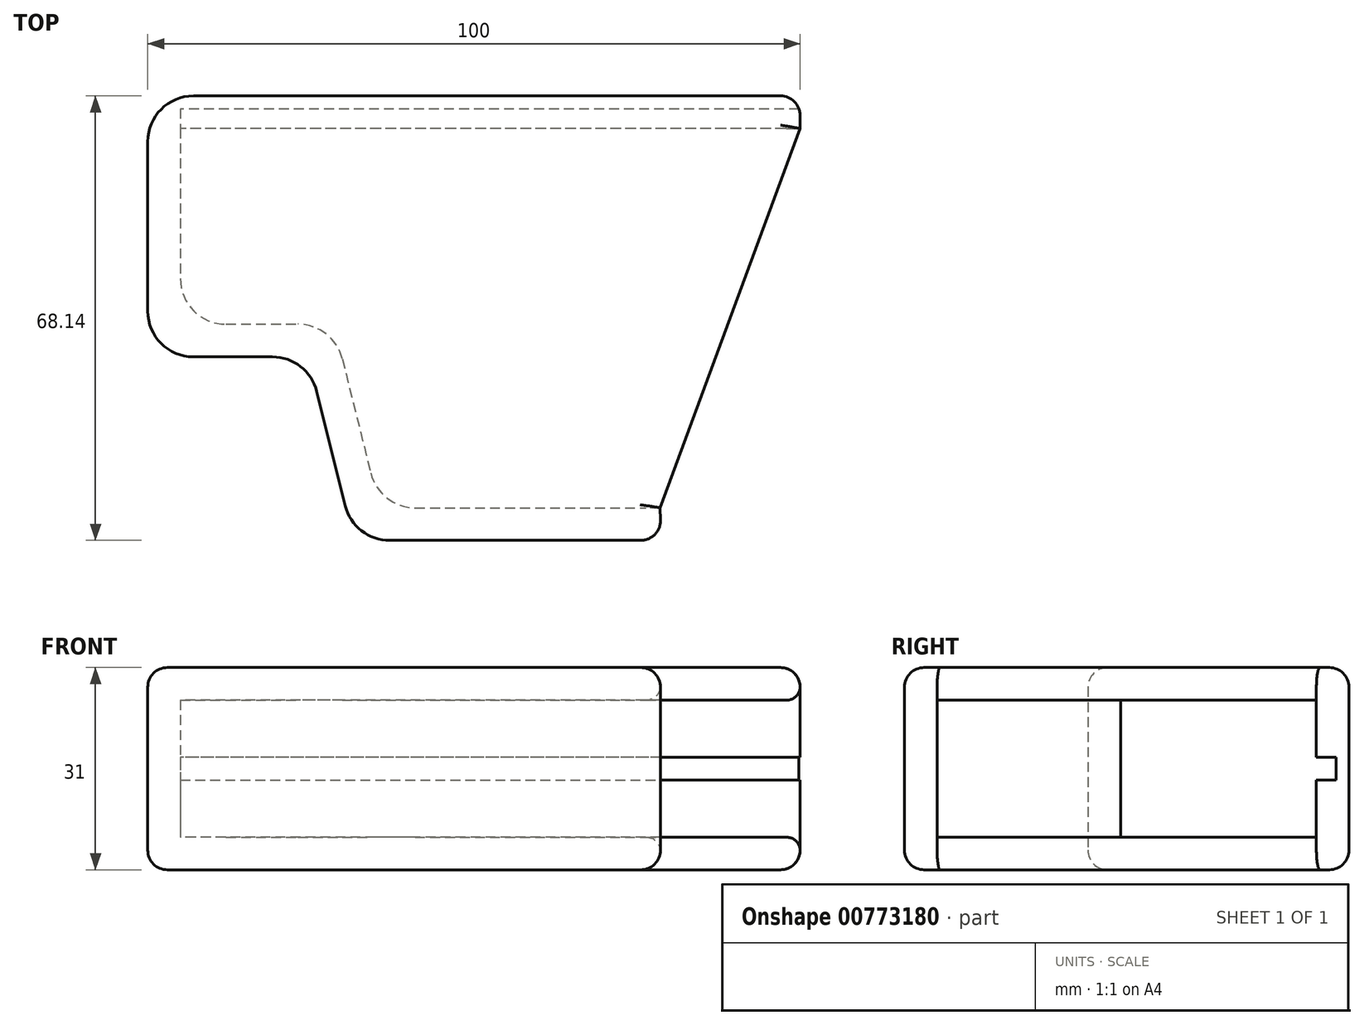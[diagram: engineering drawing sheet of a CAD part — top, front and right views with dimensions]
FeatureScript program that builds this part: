
annotation { "Feature Type Name" : "Feature", "Feature Type Description" : "" }
export const myFeature = defineFeature(function(context is Context, id is Id, definition is map)
    precondition{}
    {
        {
            var Q0;
            Q0=qCreatedBy(makeId("Top.planeOp"),FACE);
            var sketch = newSketch(context, id + "F0", { "sketchPlane" : qUnion([Q0])});
            skLineSegment(sketch, "E0", {"start": v(71.5, 30) * mm, "end": v(-23.5, 30) * mm});
            skLineSegment(sketch, "E1", {"start": v(-23.5, 30) * mm, "end": v(-23.5, 0) * mm});
            skLineSegment(sketch, "E2", {"start": v(-23.5, 0) * mm, "end": v(0, 0) * mm});
            skLineSegment(sketch, "E3", {"start": v(0, 0) * mm, "end": v(7.01, -28.14) * mm});
            skLineSegment(sketch, "E4", {"start": v(7.01, -28.14) * mm, "end": v(50.01, -28.14) * mm});
            skLineSegment(sketch, "E5", {"start": v(71.5, 30) * mm, "end": v(71.5, 35) * mm});
            skLineSegment(sketch, "E6", {"start": v(71.5, 35) * mm, "end": v(-28.5, 35) * mm});
            skLineSegment(sketch, "E7", {"start": v(-28.5, 35) * mm, "end": v(-28.5, -5) * mm});
            skLineSegment(sketch, "E8", {"start": v(-28.5, -5) * mm, "end": v(-3.9, -5) * mm});
            skLineSegment(sketch, "E9", {"start": v(-3.9, -5) * mm, "end": v(3.1, -33.14) * mm});
            skLineSegment(sketch, "E10", {"start": v(3.1, -33.14) * mm, "end": v(50.2, -33.14) * mm});
            skLineSegment(sketch, "E11", {"start": v(50.2, -33.14) * mm, "end": v(50.01, -28.14) * mm});
            skSolve(sketch);
        }
        {
            var Q0;
            Q0 = qSketchRegion(id + "F0", true);
            extrude(context, id + "F1", {"entities" : qUnion([Q0]), "depth" : 21 * mm, "offsetDistance" : 25 * mm});
        }
        {
            var Q0;
            Q0=makeQuery(id+"F1.opExtrude","CAP_FACE",FACE,{"disambiguationData":[OSD([sQuery(id+"F0.wireOp",EDGE,"E0"),sQuery(id+"F0.wireOp",EDGE,"E1"),sQuery(id+"F0.wireOp",EDGE,"E2"),sQuery(id+"F0.wireOp",EDGE,"E3"),sQuery(id+"F0.wireOp",EDGE,"E4"),sQuery(id+"F0.wireOp",EDGE,"E5"),sQuery(id+"F0.wireOp",EDGE,"E6"),sQuery(id+"F0.wireOp",EDGE,"E7"),sQuery(id+"F0.wireOp",EDGE,"E8"),sQuery(id+"F0.wireOp",EDGE,"E9"),sQuery(id+"F0.wireOp",EDGE,"E10"),sQuery(id+"F0.wireOp",EDGE,"E11")])],"isStart":true});
            var sketch = newSketch(context, id + "F2", { "sketchPlane" : qUnion([Q0])});
            skLineSegment(sketch, "E12", {"start": v(71.5, -35) * mm, "end": v(-28.5, -35) * mm});
            skLineSegment(sketch, "E13", {"start": v(-28.5, -35) * mm, "end": v(-28.5, 5) * mm});
            skLineSegment(sketch, "E14", {"start": v(-28.5, 5) * mm, "end": v(-3.9, 5) * mm});
            skLineSegment(sketch, "E15", {"start": v(-3.9, 5) * mm, "end": v(3.1, 33.14) * mm});
            skLineSegment(sketch, "E16", {"start": v(3.1, 33.14) * mm, "end": v(50.2, 33.14) * mm});
            skLineSegment(sketch, "E17", {"start": v(50.2, 33.14) * mm, "end": v(50.01, 28.14) * mm});
            skLineSegment(sketch, "E18", {"start": v(50.01, 28.14) * mm, "end": v(71.5, -30) * mm});
            skLineSegment(sketch, "E19", {"start": v(71.5, -30) * mm, "end": v(71.5, -35) * mm});
            skSolve(sketch);
        }
        {
            var Q0;
            Q0=makeQuery(id+"F1.opExtrude","CAP_FACE",FACE,{"disambiguationData":[OSD([sQuery(id+"F0.wireOp",EDGE,"E0"),sQuery(id+"F0.wireOp",EDGE,"E1"),sQuery(id+"F0.wireOp",EDGE,"E2"),sQuery(id+"F0.wireOp",EDGE,"E3"),sQuery(id+"F0.wireOp",EDGE,"E4"),sQuery(id+"F0.wireOp",EDGE,"E5"),sQuery(id+"F0.wireOp",EDGE,"E6"),sQuery(id+"F0.wireOp",EDGE,"E7"),sQuery(id+"F0.wireOp",EDGE,"E8"),sQuery(id+"F0.wireOp",EDGE,"E9"),sQuery(id+"F0.wireOp",EDGE,"E10"),sQuery(id+"F0.wireOp",EDGE,"E11")])],"isStart":false});
            var sketch = newSketch(context, id + "F3", { "sketchPlane" : qUnion([Q0])});
            skLineSegment(sketch, "E20", {"start": v(-28.5, 35) * mm, "end": v(71.5, 35) * mm});
            skLineSegment(sketch, "E21", {"start": v(50.01, -28.14) * mm, "end": v(50.2, -33.14) * mm});
            skLineSegment(sketch, "E22", {"start": v(50.2, -33.14) * mm, "end": v(3.1, -33.14) * mm});
            skLineSegment(sketch, "E23", {"start": v(3.1, -33.14) * mm, "end": v(-3.9, -5) * mm});
            skLineSegment(sketch, "E24", {"start": v(-3.9, -5) * mm, "end": v(-28.5, -5) * mm});
            skLineSegment(sketch, "E25", {"start": v(-28.5, -5) * mm, "end": v(-28.5, 35) * mm});
            skLineSegment(sketch, "E26", {"start": v(50.01, -28.14) * mm, "end": v(71.5, 30) * mm});
            skLineSegment(sketch, "E27", {"start": v(71.5, 30) * mm, "end": v(71.5, 35) * mm});
            skSolve(sketch);
        }
        {
            var Q0;
            Q0 = qSketchRegion(id + "F3", true);
            extrude(context, id + "F4", {"entities" : qUnion([Q0]), "operationType" : NewBodyOperationType.ADD, "depth" : 5 * mm, "offsetDistance" : 25 * mm});
        }
        {
            var Q0;
            Q0 = qSketchRegion(id + "F2", true);
            extrude(context, id + "F5", {"entities" : qUnion([Q0]), "operationType" : NewBodyOperationType.ADD, "depth" : 5 * mm, "offsetDistance" : 25 * mm});
        }
        {
            var Q0;
            Q0=makeQuery(id+"F1.opExtrude","SWEPT_EDGE",EDGE,{"disambiguationData":[OSD([sQuery(id+"F0.wireOp",EDGE,"E2"),sQuery(id+"F0.wireOp",EDGE,"E3")])]});
            var Q1;
            Q1=makeQuery(id+"F1.opExtrude","SWEPT_EDGE",EDGE,{"disambiguationData":[OSD([sQuery(id+"F0.wireOp",EDGE,"E8"),sQuery(id+"F0.wireOp",EDGE,"E9")])]});
            var Q2;
            Q2=makeQuery(id+"F1.opExtrude","SWEPT_EDGE",EDGE,{"disambiguationData":[OSD([sQuery(id+"F0.wireOp",EDGE,"E3"),sQuery(id+"F0.wireOp",EDGE,"E4")])]});
            var Q3;
            Q3=makeQuery(id+"F1.opExtrude","SWEPT_EDGE",EDGE,{"disambiguationData":[OSD([sQuery(id+"F0.wireOp",EDGE,"E9"),sQuery(id+"F0.wireOp",EDGE,"E10")])]});
            var Q4;
            Q4=makeQuery(id+"F1.opExtrude","SWEPT_EDGE",EDGE,{"disambiguationData":[OSD([sQuery(id+"F0.wireOp",EDGE,"E7"),sQuery(id+"F0.wireOp",EDGE,"E8")])]});
            var Q5;
            Q5=makeQuery(id+"F1.opExtrude","SWEPT_EDGE",EDGE,{"disambiguationData":[OSD([sQuery(id+"F0.wireOp",EDGE,"E6"),sQuery(id+"F0.wireOp",EDGE,"E7")])]});
            var Q6;
            Q6=makeQuery(id+"F1.opExtrude","SWEPT_EDGE",EDGE,{"disambiguationData":[OSD([sQuery(id+"F0.wireOp",EDGE,"E1"),sQuery(id+"F0.wireOp",EDGE,"E2")])]});
            fillet(context, id + "F6", {"entities" : qUnion([Q0, Q1, Q2, Q3, Q4, Q5, Q6]), "radius" : 7 * mm, "tangentPropagation" : true, "allowEdgeOverflow" : false});
        }
        {
            var Q0;
            Q0=makeQuery(id+"F4.opExtrude","CAP_EDGE",EDGE,{"disambiguationData":[OSD([sQuery(id+"F3.wireOp",EDGE,"E20")])],"isStart":false});
            var Q1;
            Q1=makeQuery(id+"F5.opExtrude","CAP_EDGE",EDGE,{"disambiguationData":[OSD([sQuery(id+"F2.wireOp",EDGE,"E12")])],"isStart":false});
            var Q2;
            Q2=makeQuery(id+"F5.boolean.opBoolean","MERGE",EDGE,{"derivedFrom":[makeQuery(id+"F4.boolean.opBoolean","MERGE",EDGE,{"derivedFrom":[makeQuery(id+"F1.opExtrude","SWEPT_EDGE",EDGE,{"disambiguationData":[OSD([sQuery(id+"F0.wireOp",EDGE,"E5"),sQuery(id+"F0.wireOp",EDGE,"E6")])]}),makeQuery(id+"F4.opExtrude","SWEPT_EDGE",EDGE,{"disambiguationData":[OSD([sQuery(id+"F3.wireOp",EDGE,"E20"),sQuery(id+"F3.wireOp",EDGE,"E27")])]})]}),makeQuery(id+"F5.opExtrude","SWEPT_EDGE",EDGE,{"disambiguationData":[OSD([sQuery(id+"F2.wireOp",EDGE,"E12"),sQuery(id+"F2.wireOp",EDGE,"E19")])]})]});
            var Q3;
            Q3=makeQuery(id+"F4.opExtrude","CAP_FACE",FACE,{"disambiguationData":[OSD([sQuery(id+"F3.wireOp",EDGE,"E20"),sQuery(id+"F3.wireOp",EDGE,"E21"),sQuery(id+"F3.wireOp",EDGE,"E22"),sQuery(id+"F3.wireOp",EDGE,"E23"),sQuery(id+"F3.wireOp",EDGE,"E24"),sQuery(id+"F3.wireOp",EDGE,"E25"),sQuery(id+"F3.wireOp",EDGE,"E26"),sQuery(id+"F3.wireOp",EDGE,"E27")])],"isStart":false});
            var Q4;
            Q4=makeQuery(id+"F5.opExtrude","CAP_FACE",FACE,{"disambiguationData":[OSD([sQuery(id+"F2.wireOp",EDGE,"E12"),sQuery(id+"F2.wireOp",EDGE,"E13"),sQuery(id+"F2.wireOp",EDGE,"E14"),sQuery(id+"F2.wireOp",EDGE,"E15"),sQuery(id+"F2.wireOp",EDGE,"E16"),sQuery(id+"F2.wireOp",EDGE,"E17"),sQuery(id+"F2.wireOp",EDGE,"E18"),sQuery(id+"F2.wireOp",EDGE,"E19")])],"isStart":false});
            var Q5;
            Q5=makeQuery(id+"F5.boolean.opBoolean","MERGE",EDGE,{"derivedFrom":[makeQuery(id+"F4.boolean.opBoolean","MERGE",EDGE,{"derivedFrom":[makeQuery(id+"F1.opExtrude","SWEPT_EDGE",EDGE,{"disambiguationData":[OSD([sQuery(id+"F0.wireOp",EDGE,"E10"),sQuery(id+"F0.wireOp",EDGE,"E11")])]}),makeQuery(id+"F4.opExtrude","SWEPT_EDGE",EDGE,{"disambiguationData":[OSD([sQuery(id+"F3.wireOp",EDGE,"E21"),sQuery(id+"F3.wireOp",EDGE,"E22")])]})]}),makeQuery(id+"F5.opExtrude","SWEPT_EDGE",EDGE,{"disambiguationData":[OSD([sQuery(id+"F2.wireOp",EDGE,"E16"),sQuery(id+"F2.wireOp",EDGE,"E17")])]})]});
            fillet(context, id + "F7", {"entities" : qUnion([Q0, Q1, Q2, Q3, Q4, Q5]), "radius" : 3 * mm, "tangentPropagation" : true, "allowEdgeOverflow" : false});
        }
        {
            var Q0;
            Q0=makeQuery(id+"F1.opExtrude","SWEPT_FACE",FACE,{"disambiguationData":[OSD([sQuery(id+"F0.wireOp",EDGE,"E0")])]});
            var sketch = newSketch(context, id + "F8", { "sketchPlane" : qUnion([Q0])});
            skLineSegment(sketch, "E28", {"start": v(-23.5, 10.5) * mm, "end": v(-23.5, 12.25) * mm});
            skLineSegment(sketch, "E29", {"start": v(-23.5, 12.25) * mm, "end": v(-23.5, 8.75) * mm});
            skLineSegment(sketch, "E30", {"start": v(-23.5, 8.75) * mm, "end": v(74.16, 8.75) * mm});
            skLineSegment(sketch, "E31", {"start": v(74.16, 8.75) * mm, "end": v(74.16, 12.25) * mm});
            skLineSegment(sketch, "E32", {"start": v(74.16, 12.25) * mm, "end": v(-23.5, 12.25) * mm});
            skSolve(sketch);
        }
        {
            var Q0;
            Q0 = qSketchRegion(id + "F8", true);
            extrude(context, id + "F9", {"entities" : qUnion([Q0]), "operationType" : NewBodyOperationType.REMOVE, "oppositeDirection" : true, "depth" : 3 * mm, "offsetDistance" : 25 * mm});
        }
        {
            var Q0;
            Q0=makeQuery(id+"F4.opExtrude","CAP_EDGE",EDGE,{"disambiguationData":[OSD([sQuery(id+"F3.wireOp",EDGE,"E26")])],"isStart":true});
            var Q1;
            Q1=makeQuery(id+"F5.opExtrude","CAP_EDGE",EDGE,{"disambiguationData":[OSD([sQuery(id+"F2.wireOp",EDGE,"E18")])],"isStart":true});
            fillet(context, id + "F10", {"entities" : qUnion([Q0, Q1]), "radius" : 2 * mm, "tangentPropagation" : true, "allowEdgeOverflow" : false});
        }
    });
